# Revit family: 306_8a3b6224d82c423d8aa13aa47e60fe
name_source: partatom
category: Pipe Accessories
units: mm (PartAtom-declared; Revit-internal decimal feet)

## family parameters
Always vertical = Yes
Cut with Voids When Loaded = No
Part Type = Valve - Breaks Into
Round Connector Dimension = Use Diameter
Shared = No
Work Plane-Based = No

## types (5) — shared parameters
CAT0 = Yes
Description = 3-way Control valve VLF135, PN6 flange
L2D = 150 mm
L2D_Min = 3048 mm
MC = No
Manufacturer = ESBE
QmdConnectorList = 301;D;302;D
R9 = 4 mm  [stored 0.0131234 ft]
URL = http://www.esbe.eu
W2D = 20 mm  [stored 0.0656168 ft]
X1 = 2 mm  [stored 0.00656168 ft]
Z10 = 2 mm  [stored 0.00656168 ft]
Z4 = 17 mm  [stored 0.0557743 ft]
Z7 = 3 mm  [stored 0.00984252 ft]
Z8 = 13 mm
Z9 = 4 mm  [stored 0.0131234 ft]
magiPartTypeId = 306
magiProductFamilyId = 8a3b6224d82c423d8aa13aa47e60fe

## per-type parameters (varying)
- VLF135 PN6 FLÄNS DN20-6,3: CenSd_R6_6=12 mm  [stored 0.0393701 ft]; D=20 mm; D2=29 mm; D3=27 mm  [stored 0.0885827 ft]; D4=23 mm; FDT2=45 mm; H3=41 mm; H4=75 mm; HCDT2=24 mm; L4=131 mm; LT2=75 mm; R1=15 mm  [stored 0.0492126 ft]; R2=18 mm; R3=25 mm  [stored 0.082021 ft]; R4=20 mm  [stored 0.0656168 ft]; R5=16 mm; R6=14 mm  [stored 0.0459318 ft]; R7=8 mm  [stored 0.0262467 ft]; R8=6 mm  [stored 0.019685 ft]; X2=7 mm  [stored 0.0229659 ft]; X2__ve=-7 mm; Z12=10 mm  [stored 0.0328084 ft]; Z13=5 mm  [stored 0.0164042 ft]; Z14=5 mm  [stored 0.0164042 ft]; Z14__ve=-5 mm  [stored -0.0164042 ft]; Z3=71 mm; Z5=9 mm  [stored 0.0295276 ft]; Z6=9 mm  [stored 0.0295276 ft]; magiProductId=e75cef7eec7e4c8aacd9d218e660a2
- VLF135 PN6 FLÄNS DN25-10: CenSd_R6_6=13 mm; D=25 mm; D2=31 mm; D3=32 mm  [stored 0.104987 ft]; D4=27 mm  [stored 0.0885827 ft]; FDT2=50 mm; H3=46 mm; H4=80 mm; HCDT2=29 mm; L4=140 mm; LT2=80 mm; R1=18 mm; R2=22 mm; R3=27 mm  [stored 0.0885827 ft]; R4=22 mm; R5=17 mm  [stored 0.0557743 ft]; R6=15 mm  [stored 0.0492126 ft]; R7=9 mm  [stored 0.0295276 ft]; R8=7 mm  [stored 0.0229659 ft]; X2=8 mm  [stored 0.0262467 ft]; X2__ve=-8 mm; Z12=11 mm; Z13=5 mm  [stored 0.0164042 ft]; Z14=6 mm  [stored 0.019685 ft]; Z14__ve=-6 mm; Z3=78 mm; Z5=9 mm  [stored 0.0295276 ft]; Z6=9 mm  [stored 0.0295276 ft]; magiProductId=252346e9126440bcb217554d623be7
- VLF135 PN6 FLÄNS DN32-16: CenSd_R6_6=14 mm  [stored 0.0459318 ft]; D=32 mm; D2=35 mm; D3=38 mm; D4=32 mm  [stored 0.104987 ft]; FDT2=60 mm; H3=60 mm; H4=90 mm; HCDT2=35 mm; L4=158 mm; LT2=90 mm; R1=21 mm; R2=26 mm; R3=31 mm; R4=24 mm; R5=20 mm  [stored 0.0656168 ft]; R6=17 mm  [stored 0.0557743 ft]; R7=10 mm  [stored 0.0328084 ft]; R8=7 mm  [stored 0.0229659 ft]; X2=9 mm  [stored 0.0295276 ft]; X2__ve=-9 mm; Z12=12 mm  [stored 0.0393701 ft]; Z13=6 mm  [stored 0.019685 ft]; Z14=8 mm  [stored 0.0262467 ft]; Z14__ve=-8 mm; Z3=94 mm; Z5=8 mm  [stored 0.0262467 ft]; Z6=8 mm  [stored 0.0262467 ft]; magiProductId=ff309e7486274a23b0b7e973354af0
- VLF135 PN6 FLÄNS DN40-25: CenSd_R6_6=16 mm; D=40 mm; D2=39 mm; D3=43 mm; D4=37 mm; FDT2=65 mm; H3=61 mm; H4=100 mm; HCDT2=40 mm; L4=176 mm; LT2=100 mm; R1=24 mm; R2=30 mm  [stored 0.0984252 ft]; R3=34 mm; R4=27 mm  [stored 0.0885827 ft]; R5=22 mm; R6=18 mm; R7=11 mm; R8=8 mm  [stored 0.0262467 ft]; X2=10 mm  [stored 0.0328084 ft]; X2__ve=-10 mm  [stored -0.0328084 ft]; Z12=14 mm  [stored 0.0459318 ft]; Z13=7 mm  [stored 0.0229659 ft]; Z14=8 mm  [stored 0.0262467 ft]; Z14__ve=-8 mm; Z3=100 mm; Z5=9 mm  [stored 0.0295276 ft]; Z6=9 mm  [stored 0.0295276 ft]; magiProductId=793520d6363442ac9fb912cdc7b4f4
- VLF135 PN6 FLÄNS DN50-38: CenSd_R6_6=18 mm; D=50 mm; D2=45 mm; D3=48 mm; D4=41 mm; FDT2=70 mm; H3=76 mm; H4=115 mm; HCDT2=45 mm; L4=203 mm; LT2=115 mm; R1=27 mm  [stored 0.0885827 ft]; R2=33 mm; R3=39 mm; R4=31 mm; R5=25 mm  [stored 0.082021 ft]; R6=21 mm; R7=13 mm; R8=10 mm  [stored 0.0328084 ft]; X2=11 mm; X2__ve=-11 mm; Z12=16 mm; Z13=8 mm  [stored 0.0262467 ft]; Z14=10 mm  [stored 0.0328084 ft]; Z14__ve=-10 mm  [stored -0.0328084 ft]; Z3=120 mm; Z5=9 mm  [stored 0.0295276 ft]; Z6=9 mm  [stored 0.0295276 ft]; magiProductId=71fc7444374f4c00b1f1dd7a4e270d

note: column(s) folded — value = type name in every type: MC Product Code

note: [stored X ft] marks values corroborated as IEEE doubles in the binary element streams (Revit-internal decimal feet)

## geometry (parser evidence)
native form markers: Sweep x3
no freeform markers — native parametric forms only
